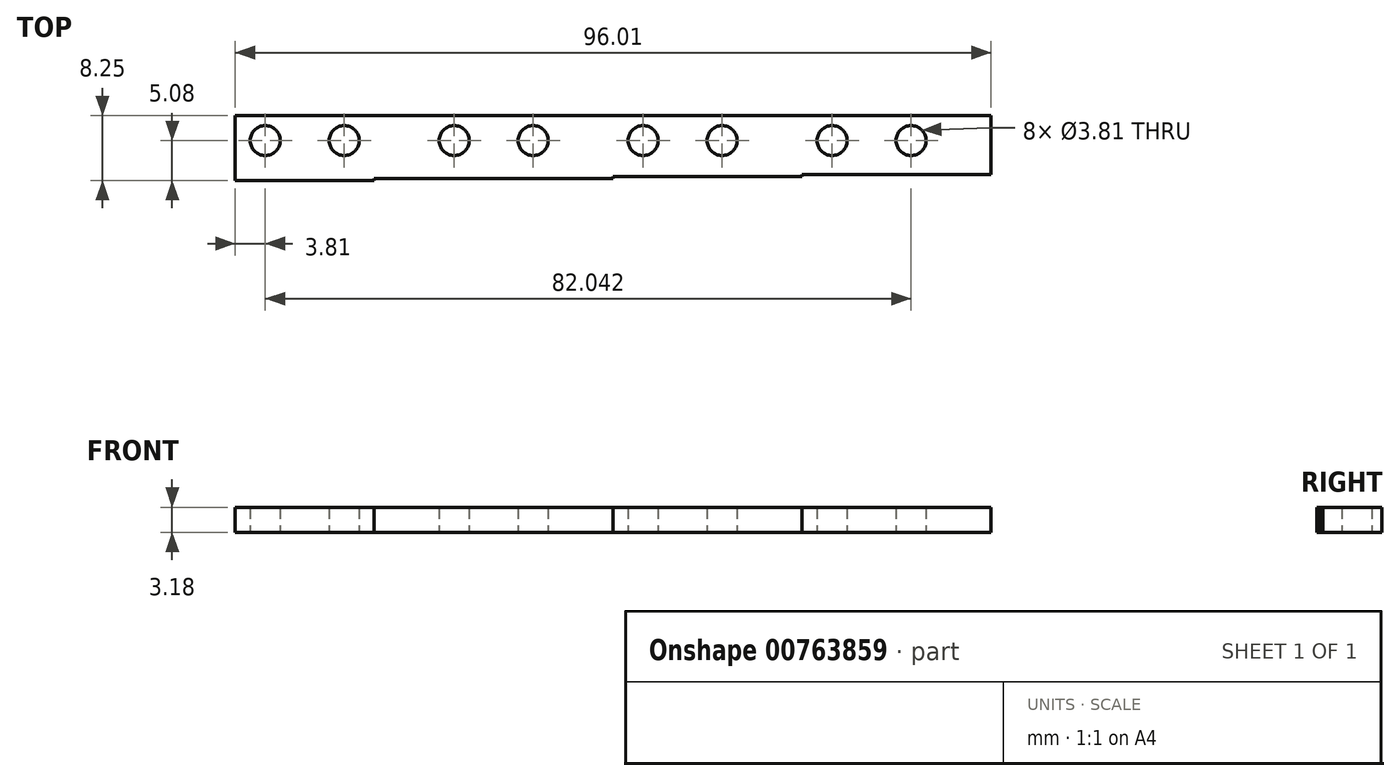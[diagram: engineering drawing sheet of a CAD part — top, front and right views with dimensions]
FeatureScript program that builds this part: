
annotation { "Feature Type Name" : "Feature", "Feature Type Description" : "" }
export const myFeature = defineFeature(function(context is Context, id is Id, definition is map)
    precondition{}
    {
        {
            var Q0;
            Q0=qCreatedBy(makeId("Top.planeOp"),FACE);
            var sketch = newSketch(context, id + "F0", { "sketchPlane" : qUnion([Q0])});
            skLineSegment(sketch, "E0.bottom", {"start": v(8.83, -3.18) * mm, "end": v(-8.83, -3.17) * mm});
            skLineSegment(sketch, "E0.top", {"start": v(8.83, 3.17) * mm, "end": v(-8.83, 3.18) * mm});
            skLineSegment(sketch, "E0.left", {"start": v(8.83, -3.18) * mm, "end": v(8.83, 3.17) * mm});
            skLineSegment(sketch, "E0.right", {"start": v(-8.83, -3.17) * mm, "end": v(-8.83, 3.18) * mm});
            skPoint(sketch, "E0.middle", {"position": v(0, 0) * mm});
            skCircle(sketch, "E1", {"center": v(-5.02, 0) * mm, "radius": 1.9 * mm});
            skCircle(sketch, "E2", {"center": v(5.02, 0) * mm, "radius": 1.9 * mm});
            skLineSegment(sketch, "E3.bottom", {"start": v(-8.83, -3.17) * mm, "end": v(8.83, -3.17) * mm});
            skLineSegment(sketch, "E3.top", {"start": v(-8.83, -4.83) * mm, "end": v(8.83, -4.83) * mm});
            skLineSegment(sketch, "E3.left", {"start": v(-8.83, -3.17) * mm, "end": v(-8.83, -4.83) * mm});
            skLineSegment(sketch, "E3.right", {"start": v(8.83, -3.17) * mm, "end": v(8.83, -4.83) * mm});
            skLineSegment(sketch, "E4.bottom", {"start": v(8.83, 3.17) * mm, "end": v(15.18, 3.17) * mm});
            skLineSegment(sketch, "E4.top", {"start": v(8.83, -4.83) * mm, "end": v(15.18, -4.83) * mm});
            skLineSegment(sketch, "E4.left", {"start": v(8.83, 3.17) * mm, "end": v(8.83, -4.83) * mm});
            skLineSegment(sketch, "E4.right", {"start": v(15.18, 3.17) * mm, "end": v(15.18, -4.83) * mm});
            skLineSegment(sketch, "E5", {"start": v(12, 3.17) * mm, "end": v(12, -4.83) * mm});
            skLineSegment(sketch, "E6.MirrorCS", {"start": v(15.18, -3.17) * mm, "end": v(15.18, -4.83) * mm});
            skLineSegment(sketch, "E7.MirrorCS", {"start": v(15.18, -3.18) * mm, "end": v(32.83, -3.17) * mm});
            skLineSegment(sketch, "E8.MirrorCS", {"start": v(15.18, -3.18) * mm, "end": v(15.18, 3.17) * mm});
            skLineSegment(sketch, "E9.MirrorCS", {"start": v(15.18, 3.17) * mm, "end": v(32.83, 3.18) * mm});
            skLineSegment(sketch, "E10.MirrorCS", {"start": v(32.83, -3.17) * mm, "end": v(15.18, -3.17) * mm});
            skCircle(sketch, "E11.MirrorC", {"center": v(18.99, 0) * mm, "radius": 1.9 * mm});
            skPoint(sketch, "E12.MirrorP", {"position": v(24, 0) * mm});
            skLineSegment(sketch, "E13.MirrorCS", {"start": v(32.83, -3.17) * mm, "end": v(32.83, 3.18) * mm});
            skCircle(sketch, "E14.MirrorC", {"center": v(29.02, 0) * mm, "radius": 1.9 * mm});
            skLineSegment(sketch, "E15.bottom", {"start": v(15.18, -3.17) * mm, "end": v(32.83, -3.17) * mm});
            skLineSegment(sketch, "E15.top", {"start": v(15.18, -4.57) * mm, "end": v(32.83, -4.57) * mm});
            skLineSegment(sketch, "E15.left", {"start": v(15.18, -3.17) * mm, "end": v(15.18, -4.57) * mm});
            skLineSegment(sketch, "E15.right", {"start": v(32.83, -3.18) * mm, "end": v(32.83, -4.57) * mm});
            skLineSegment(sketch, "E16.bottom", {"start": v(-8.83, 3.18) * mm, "end": v(-12, 3.18) * mm});
            skLineSegment(sketch, "E16.top", {"start": v(-8.83, -4.83) * mm, "end": v(-12, -4.83) * mm});
            skLineSegment(sketch, "E16.left", {"start": v(-8.83, 3.18) * mm, "end": v(-8.83, -4.83) * mm});
            skLineSegment(sketch, "E16.right", {"start": v(-12, 3.17) * mm, "end": v(-12, -4.83) * mm});
            skLineSegment(sketch, "E17.MirrorCS", {"start": v(-32.83, -3.18) * mm, "end": v(-32.83, 3.17) * mm});
            skLineSegment(sketch, "E18.MirrorCS", {"start": v(-32.83, -3.18) * mm, "end": v(-15.18, -3.18) * mm});
            skLineSegment(sketch, "E19.MirrorCS", {"start": v(-15.18, 3.17) * mm, "end": v(-15.18, -4.83) * mm});
            skLineSegment(sketch, "E20.MirrorCS", {"start": v(-32.83, 3.17) * mm, "end": v(-15.18, 3.17) * mm});
            skLineSegment(sketch, "E21.MirrorCS", {"start": v(-15.18, -4.83) * mm, "end": v(-12, -4.83) * mm});
            skLineSegment(sketch, "E22.MirrorCS", {"start": v(-15.18, -3.18) * mm, "end": v(-32.83, -3.18) * mm});
            skLineSegment(sketch, "E23.MirrorCS", {"start": v(-15.18, -3.18) * mm, "end": v(-15.18, -4.83) * mm});
            skCircle(sketch, "E24.MirrorC", {"center": v(-18.99, 0) * mm, "radius": 1.9 * mm});
            skLineSegment(sketch, "E25.MirrorCS", {"start": v(-15.18, -3.18) * mm, "end": v(-15.18, 3.17) * mm});
            skCircle(sketch, "E26.MirrorC", {"center": v(-29.02, 0) * mm, "radius": 1.9 * mm});
            skPoint(sketch, "E27.MirrorP", {"position": v(-24, 0) * mm});
            skLineSegment(sketch, "E28.MirrorCS", {"start": v(-15.18, 3.17) * mm, "end": v(-12, 3.18) * mm});
            skLineSegment(sketch, "E29.top", {"start": v(-32.83, -5.08) * mm, "end": v(-15.18, -5.08) * mm});
            skLineSegment(sketch, "E29.left", {"start": v(-32.83, -3.18) * mm, "end": v(-32.83, -5.08) * mm});
            skLineSegment(sketch, "E29.right", {"start": v(-15.18, -3.18) * mm, "end": v(-15.18, -5.08) * mm});
            skLineSegment(sketch, "E30.bottom", {"start": v(32.83, 3.18) * mm, "end": v(36, 3.18) * mm});
            skLineSegment(sketch, "E30.top", {"start": v(32.83, -4.57) * mm, "end": v(36, -4.57) * mm});
            skLineSegment(sketch, "E30.left", {"start": v(32.83, 3.18) * mm, "end": v(32.83, -4.57) * mm});
            skLineSegment(sketch, "E30.right", {"start": v(36, 3.18) * mm, "end": v(36, -4.57) * mm});
            skLineSegment(sketch, "E31.MirrorCS", {"start": v(39.18, -3.18) * mm, "end": v(39.18, -4.57) * mm});
            skLineSegment(sketch, "E32.MirrorCS", {"start": v(56.83, -3.17) * mm, "end": v(39.18, -3.17) * mm});
            skLineSegment(sketch, "E33.MirrorCS", {"start": v(39.18, -3.17) * mm, "end": v(39.18, 3.18) * mm});
            skLineSegment(sketch, "E34.MirrorCS", {"start": v(39.18, -3.17) * mm, "end": v(56.83, -3.17) * mm});
            skLineSegment(sketch, "E35.MirrorCS", {"start": v(56.83, -3.17) * mm, "end": v(56.83, 3.18) * mm});
            skCircle(sketch, "E36.MirrorC", {"center": v(42.99, 0) * mm, "radius": 1.9 * mm});
            skLineSegment(sketch, "E37.MirrorCS", {"start": v(39.18, 3.18) * mm, "end": v(36, 3.18) * mm});
            skLineSegment(sketch, "E38.MirrorCS", {"start": v(39.18, -4.57) * mm, "end": v(36, -4.57) * mm});
            skCircle(sketch, "E39.MirrorC", {"center": v(53.02, 0) * mm, "radius": 1.9 * mm});
            skPoint(sketch, "E40.MirrorP", {"position": v(48, 0) * mm});
            skLineSegment(sketch, "E41.MirrorCS", {"start": v(56.83, 3.18) * mm, "end": v(39.18, 3.18) * mm});
            skLineSegment(sketch, "E42.MirrorCS", {"start": v(39.18, 3.18) * mm, "end": v(39.18, -4.57) * mm});
            skLineSegment(sketch, "E43.bottom", {"start": v(39.18, -3.18) * mm, "end": v(56.83, -3.18) * mm});
            skLineSegment(sketch, "E43.top", {"start": v(39.18, -4.32) * mm, "end": v(56.83, -4.32) * mm});
            skLineSegment(sketch, "E43.left", {"start": v(39.18, -3.18) * mm, "end": v(39.18, -4.32) * mm});
            skLineSegment(sketch, "E43.right", {"start": v(56.83, -3.17) * mm, "end": v(56.83, -4.32) * mm});
            skLineSegment(sketch, "E44.bottom", {"start": v(56.83, 3.18) * mm, "end": v(63.18, 3.18) * mm});
            skLineSegment(sketch, "E44.top", {"start": v(56.83, -4.32) * mm, "end": v(63.18, -4.32) * mm});
            skLineSegment(sketch, "E44.left", {"start": v(56.83, 3.18) * mm, "end": v(56.83, -4.32) * mm});
            skLineSegment(sketch, "E44.right", {"start": v(63.18, 3.17) * mm, "end": v(63.18, -4.32) * mm});
            skSolve(sketch);
        }
        {
            var Q0;
            Q0 = qSketchRegion(id + "F0", true);
            extrude(context, id + "F1", {"entities" : qUnion([Q0]), "depth" : 3.17 * mm, "offsetDistance" : 25.4 * mm});
        }
    });
